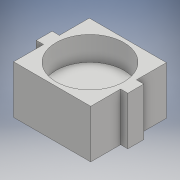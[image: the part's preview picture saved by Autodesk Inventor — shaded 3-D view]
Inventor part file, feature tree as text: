
AUTODESK INVENTOR PART (.ipt)
format: ipt  version: 2018 (Build 220112000, 112)  size: 114,688 bytes
history: native  units: mm
features: extrude x2, sketch x2
ambient origin geometry x8: Origin, YZ Plane, XZ Plane, XY Plane, X Axis, Y Axis, Z Axis, Center Point
bodies: Solid1 (feature_tree)
feature tree (4):
  extrude  "Extrusion1"  Depth=15.7mm
  extrude  "Extrusion2"  Depth=3.3mm
  sketch  "Sketch1"  dims[d0=16.0mm d1=15.7mm]
  sketch  "Sketch2"  dims[d2=19.0mm d3=3.3mm d4=10.0mm d5=0.0mm d6=14.1mm d7=5.0mm d8=0.0mm]
